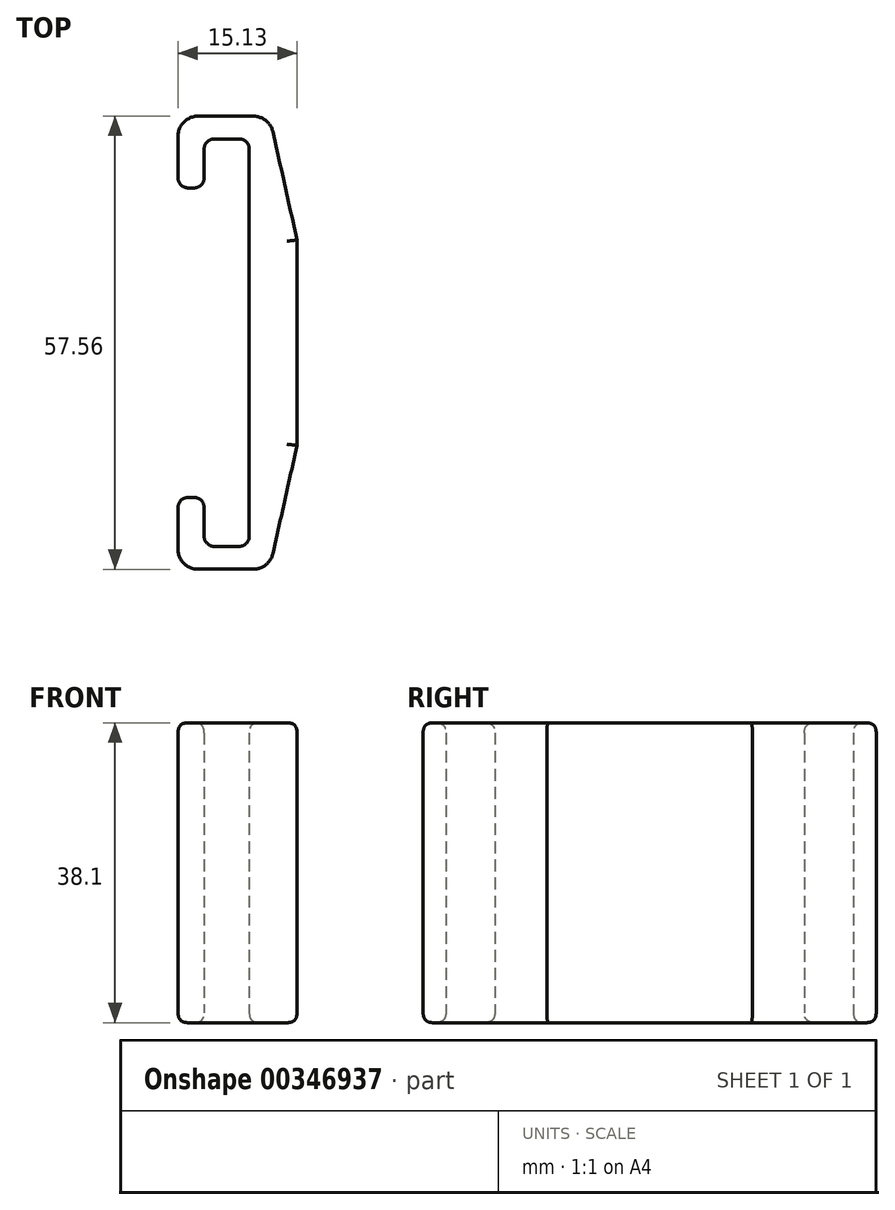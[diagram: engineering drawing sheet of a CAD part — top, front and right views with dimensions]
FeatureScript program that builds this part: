
annotation { "Feature Type Name" : "Feature", "Feature Type Description" : "" }
export const myFeature = defineFeature(function(context is Context, id is Id, definition is map)
    precondition{}
    {
        {
            var Q0;
            Q0=qCreatedBy(makeId("Top.planeOp"),FACE);
            var sketch = newSketch(context, id + "F0", { "sketchPlane" : qUnion([Q0])});
            skLineSegment(sketch, "E0", {"start": v(-15.92, -19.98) * mm, "end": v(-12.6, -19.98) * mm});
            skLineSegment(sketch, "E1", {"start": v(-12.6, -19.98) * mm, "end": v(-12.6, -26.2) * mm});
            skLineSegment(sketch, "E2", {"start": v(-6.87, -26.2) * mm, "end": v(-6.87, 0) * mm});
            skLineSegment(sketch, "E3", {"start": v(-15.92, -19.98) * mm, "end": v(-15.92, -29.1) * mm});
            skLineSegment(sketch, "E4", {"start": v(-3.9, -29.1) * mm, "end": v(-0.8, -26.06) * mm});
            skLineSegment(sketch, "E5", {"start": v(-0.8, -26.06) * mm, "end": v(-0.8, 0) * mm});
            skLineSegment(sketch, "E6.MirrorCS", {"start": v(-3.9, 28.46) * mm, "end": v(-0.8, 25.42) * mm});
            skLineSegment(sketch, "E7.MirrorCS", {"start": v(-15.92, 19.35) * mm, "end": v(-15.92, 28.46) * mm});
            skLineSegment(sketch, "E8.MirrorCS", {"start": v(-12.6, 19.35) * mm, "end": v(-12.6, 25.56) * mm});
            skLineSegment(sketch, "E9.MirrorCS", {"start": v(-15.92, 19.35) * mm, "end": v(-12.6, 19.35) * mm});
            skLineSegment(sketch, "E10.MirrorCS", {"start": v(-15.92, 19.35) * mm, "end": v(-15.92, 25.56) * mm});
            skLineSegment(sketch, "E11", {"start": v(-6.87, 25.56) * mm, "end": v(-6.87, 0) * mm});
            skLineSegment(sketch, "E12", {"start": v(-0.8, 25.42) * mm, "end": v(-0.8, 0) * mm});
            skLineSegment(sketch, "E13", {"start": v(-15.92, 28.46) * mm, "end": v(-3.9, 28.46) * mm});
            skLineSegment(sketch, "E14", {"start": v(-6.87, 25.56) * mm, "end": v(-12.6, 25.56) * mm});
            skLineSegment(sketch, "E15", {"start": v(-12.6, -26.2) * mm, "end": v(-6.87, -26.2) * mm});
            skLineSegment(sketch, "E16", {"start": v(-15.92, -29.1) * mm, "end": v(-3.9, -29.1) * mm});
            skSolve(sketch);
        }
        {
            var Q0;
            Q0=makeQuery(id+"F0.imprint","IMPRINT",FACE,{"disambiguationData":[TD([[makeQuery(id+"F0.imprint","IMPRINT",EDGE,{"derivedFrom":sQuery(id+"F0.wireOp",EDGE,"E0")}),-1.0]])]});
            extrude(context, id + "F1", {"entities" : qUnion([Q0]), "depth" : 38.1 * mm});
        }
        {
            var Q0;
            Q0=makeQuery(id+"F1.opExtrude","SWEPT_EDGE",EDGE,{"disambiguationData":[OSD([sQuery(id+"F0.wireOp",EDGE,"E6.MirrorCS"),sQuery(id+"F0.wireOp",EDGE,"E12")])]});
            var Q1;
            Q1=makeQuery(id+"F1.opExtrude","SWEPT_EDGE",EDGE,{"disambiguationData":[OSD([sQuery(id+"F0.wireOp",EDGE,"E4"),sQuery(id+"F0.wireOp",EDGE,"E5")])]});
            chamfer(context, id + "F2", {"entities" : qUnion([Q0, Q1]), "chamferType" : ChamferType.TWO_OFFSETS, "width1" : 5.08 * mm, "oppositeDirection" : false, "width2" : 12.7 * mm, "tangentPropagation" : true});
        }
        {
            var Q0;
            Q0=makeQuery(id+"F1.opExtrude","SWEPT_EDGE",EDGE,{"disambiguationData":[OSD([sQuery(id+"F0.wireOp",EDGE,"8ad12dfa-705e-40cf-afcd-3574a79ee43b0.MirrorCS"),sQuery(id+"F0.wireOp",EDGE,"34ea4ffa-25e1-4a6d-985d-f0e7a26580e20.MirrorCS")])]});
            var Q1;
            Q1=makeQuery(id+"F1.opExtrude","SWEPT_EDGE",EDGE,{"disambiguationData":[OSD([sQuery(id+"F0.wireOp",EDGE,"E10.MirrorCS"),sQuery(id+"F0.wireOp",EDGE,"E9.MirrorCS")])]});
            var Q2;
            Q2=makeQuery(id+"F1.opExtrude","SWEPT_EDGE",EDGE,{"disambiguationData":[OSD([sQuery(id+"F0.wireOp",EDGE,"E0"),sQuery(id+"F0.wireOp",EDGE,"E3")])]});
            fillet(context, id + "F3", {"entities" : qUnion([Q0, Q1, Q2]), "radius" : 1.27 * mm, "tangentPropagation" : true, "allowEdgeOverflow" : false});
        }
        {
            var Q0;
            Q0=makeQuery(id+"F1.opExtrude","SWEPT_EDGE",EDGE,{"disambiguationData":[OSD([sQuery(id+"F0.wireOp",EDGE,"E9.MirrorCS"),sQuery(id+"F0.wireOp",EDGE,"8ad12dfa-705e-40cf-afcd-3574a79ee43b0.MirrorCS")])]});
            var Q1;
            Q1=makeQuery(id+"F1.opExtrude","SWEPT_EDGE",EDGE,{"disambiguationData":[OSD([sQuery(id+"F0.wireOp",EDGE,"E0"),sQuery(id+"F0.wireOp",EDGE,"E1")])]});
            fillet(context, id + "F4", {"entities" : qUnion([Q0, Q1]), "radius" : 1.27 * mm, "tangentPropagation" : true, "allowEdgeOverflow" : false});
        }
        {
            var Q0;
            Q0=makeQuery(id+"F1.opExtrude","SWEPT_EDGE",EDGE,{"disambiguationData":[OSD([sQuery(id+"F0.wireOp",EDGE,"857682cc-67cd-4943-a00e-107c108a63800.MirrorCS"),sQuery(id+"F0.wireOp",EDGE,"E10.MirrorCS")])]});
            var Q1;
            Q1=makeQuery(id+"F1.opExtrude","SWEPT_EDGE",EDGE,{"disambiguationData":[OSD([sQuery(id+"F0.wireOp",EDGE,"E1"),sQuery(id+"F0.wireOp",EDGE,"cwueSWgR-WS5X-B3Sn-IWoJ-DJ8dUmmza1Ar")])]});
            fillet(context, id + "F5", {"entities" : qUnion([Q0, Q1]), "radius" : 1.27 * mm, "tangentPropagation" : true, "allowEdgeOverflow" : false});
        }
        {
            var Q0;
            Q0=makeQuery(id+"F1.opExtrude","SWEPT_EDGE",EDGE,{"disambiguationData":[OSD([sQuery(id+"F0.wireOp",EDGE,"857682cc-67cd-4943-a00e-107c108a63800.MirrorCS"),sQuery(id+"F0.wireOp",EDGE,"E11")])]});
            var Q1;
            Q1=makeQuery(id+"F1.opExtrude","SWEPT_EDGE",EDGE,{"disambiguationData":[OSD([sQuery(id+"F0.wireOp",EDGE,"cwueSWgR-WS5X-B3Sn-IWoJ-DJ8dUmmza1Ar"),sQuery(id+"F0.wireOp",EDGE,"E2")])]});
            fillet(context, id + "F6", {"entities" : qUnion([Q0, Q1]), "radius" : 1.27 * mm, "tangentPropagation" : true, "allowEdgeOverflow" : false});
        }
        {
            var Q0;
            Q0=makeQuery(id+"F1.opExtrude","SWEPT_EDGE",EDGE,{"disambiguationData":[OSD([sQuery(id+"F0.wireOp",EDGE,"E8.MirrorCS"),sQuery(id+"F0.wireOp",EDGE,"E14")])]});
            fillet(context, id + "F7", {"entities" : qUnion([Q0]), "radius" : 1.27 * mm, "tangentPropagation" : true, "allowEdgeOverflow" : false});
        }
        {
            var Q0;
            Q0=makeQuery(id+"F2.opChamfer","BLEND_EDGE",EDGE,{"blendedFrom":[makeQuery(id+"F1.opExtrude","SWEPT_EDGE",EDGE,{"disambiguationData":[OSD([sQuery(id+"F0.wireOp",EDGE,"E4"),sQuery(id+"F0.wireOp",EDGE,"E5")])]}),makeQuery(id+"F1.opExtrude","SWEPT_FACE",FACE,{"disambiguationData":[OSD([sQuery(id+"F0.wireOp",EDGE,"E16")])]})],"blendedInto":[makeQuery(id+"F1.opExtrude","SWEPT_FACE",FACE,{"disambiguationData":[OSD([sQuery(id+"F0.wireOp",EDGE,"E16")])]})]});
            var Q1;
            Q1=makeQuery(id+"F2.opChamfer","BLEND_EDGE",EDGE,{"blendedFrom":[makeQuery(id+"F1.opExtrude","SWEPT_EDGE",EDGE,{"disambiguationData":[OSD([sQuery(id+"F0.wireOp",EDGE,"E6.MirrorCS"),sQuery(id+"F0.wireOp",EDGE,"E12")])]}),makeQuery(id+"F1.opExtrude","SWEPT_FACE",FACE,{"disambiguationData":[OSD([sQuery(id+"F0.wireOp",EDGE,"E13")])]})],"blendedInto":[makeQuery(id+"F1.opExtrude","SWEPT_FACE",FACE,{"disambiguationData":[OSD([sQuery(id+"F0.wireOp",EDGE,"E13")])]})]});
            fillet(context, id + "F8", {"entities" : qUnion([Q0, Q1]), "radius" : 2.54 * mm, "tangentPropagation" : true, "allowEdgeOverflow" : false});
        }
        {
            var Q0;
            Q0=makeQuery(id+"F1.opExtrude","SWEPT_EDGE",EDGE,{"disambiguationData":[OSD([sQuery(id+"F0.wireOp",EDGE,"E7.MirrorCS"),sQuery(id+"F0.wireOp",EDGE,"E13")])]});
            var Q1;
            Q1=makeQuery(id+"F1.opExtrude","SWEPT_EDGE",EDGE,{"disambiguationData":[OSD([sQuery(id+"F0.wireOp",EDGE,"E3"),sQuery(id+"F0.wireOp",EDGE,"E16")])]});
            fillet(context, id + "F9", {"entities" : qUnion([Q0, Q1]), "radius" : 2.54 * mm, "tangentPropagation" : true, "allowEdgeOverflow" : false});
        }
        {
            var Q0;
            Q0=makeQuery(id+"F1.opExtrude","CAP_FACE",FACE,{"disambiguationData":[OSD([sQuery(id+"F0.wireOp",EDGE,"E0"),sQuery(id+"F0.wireOp",EDGE,"E1"),sQuery(id+"F0.wireOp",EDGE,"E2"),sQuery(id+"F0.wireOp",EDGE,"E3"),sQuery(id+"F0.wireOp",EDGE,"E4"),sQuery(id+"F0.wireOp",EDGE,"E5"),sQuery(id+"F0.wireOp",EDGE,"E7.MirrorCS"),sQuery(id+"F0.wireOp",EDGE,"E8.MirrorCS"),sQuery(id+"F0.wireOp",EDGE,"E10.MirrorCS"),sQuery(id+"F0.wireOp",EDGE,"E9.MirrorCS"),sQuery(id+"F0.wireOp",EDGE,"E6.MirrorCS"),sQuery(id+"F0.wireOp",EDGE,"E11"),sQuery(id+"F0.wireOp",EDGE,"E12"),sQuery(id+"F0.wireOp",EDGE,"E13"),sQuery(id+"F0.wireOp",EDGE,"E14"),sQuery(id+"F0.wireOp",EDGE,"E15"),sQuery(id+"F0.wireOp",EDGE,"E16")])],"isStart":false});
            var Q1;
            Q1=makeQuery(id+"F1.opExtrude","CAP_FACE",FACE,{"disambiguationData":[OSD([sQuery(id+"F0.wireOp",EDGE,"E0"),sQuery(id+"F0.wireOp",EDGE,"E1"),sQuery(id+"F0.wireOp",EDGE,"E2"),sQuery(id+"F0.wireOp",EDGE,"E3"),sQuery(id+"F0.wireOp",EDGE,"E4"),sQuery(id+"F0.wireOp",EDGE,"E5"),sQuery(id+"F0.wireOp",EDGE,"E7.MirrorCS"),sQuery(id+"F0.wireOp",EDGE,"E8.MirrorCS"),sQuery(id+"F0.wireOp",EDGE,"E10.MirrorCS"),sQuery(id+"F0.wireOp",EDGE,"E9.MirrorCS"),sQuery(id+"F0.wireOp",EDGE,"E6.MirrorCS"),sQuery(id+"F0.wireOp",EDGE,"E11"),sQuery(id+"F0.wireOp",EDGE,"E12"),sQuery(id+"F0.wireOp",EDGE,"E13"),sQuery(id+"F0.wireOp",EDGE,"E14"),sQuery(id+"F0.wireOp",EDGE,"E15"),sQuery(id+"F0.wireOp",EDGE,"E16")])],"isStart":true});
            fillet(context, id + "F10", {"entities" : qUnion([Q0, Q1]), "radius" : 1.27 * mm, "tangentPropagation" : true, "rho" : 0.5, "crossSection" : FilletCrossSection.CONIC, "allowEdgeOverflow" : false});
        }
    });
